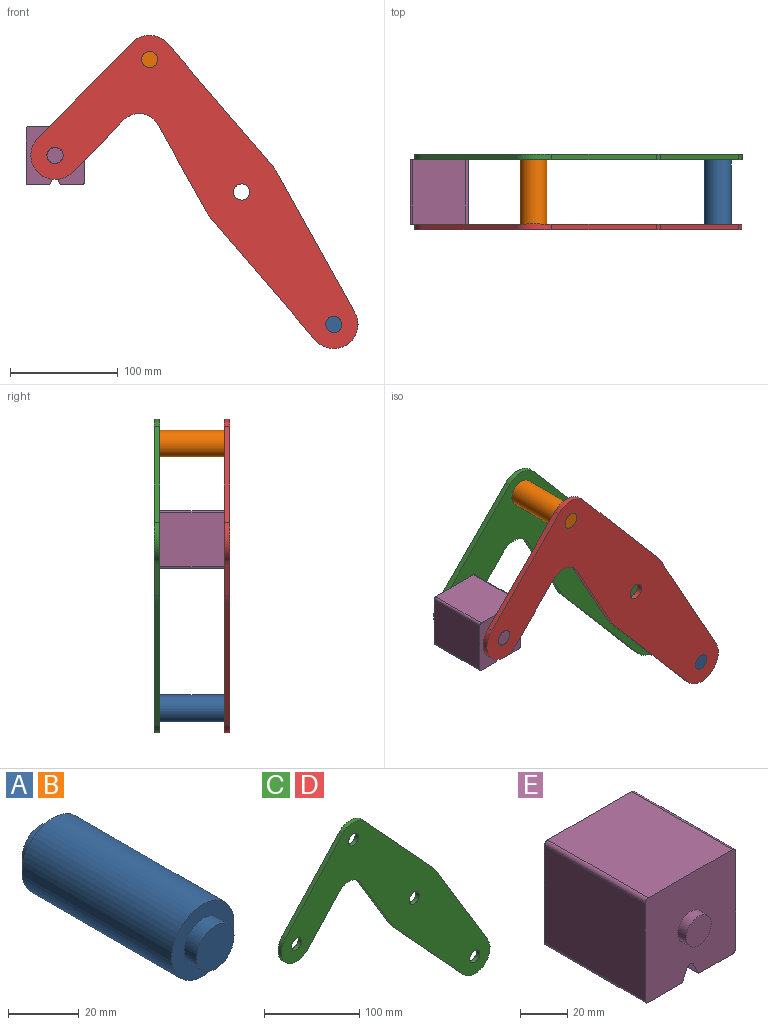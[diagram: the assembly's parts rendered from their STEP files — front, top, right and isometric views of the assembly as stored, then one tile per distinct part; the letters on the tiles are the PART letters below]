
ASSEMBLY  parts=5 mates=3
PART A: 7 faces, bbox 25x70x25 mm
  f0: cylinder r=12.5mm len=60mm, axis (0,-1,0), area 4712.4mm2, adj f2,f5
  f1: cylinder r=7.5mm len=15mm, axis (0,1,0), area 235.6mm2, adj f2,f3
  f2: plane 25x25mm, normal (0,-1,0), area 314.2mm2, adj f0,f1
  f3: plane 15x15mm, normal (0,-1,0), area 176.7mm2, adj f1
  f4: cylinder r=7.5mm len=15mm, axis (0,-1,0), area 235.6mm2, adj f5,f6
  f5: plane 25x25mm, normal (0,1,0), area 314.2mm2, adj f0,f4
  f6: plane 15x15mm, normal (0,1,0), area 176.7mm2, adj f4
PART B: same geometry as A
PART C: 18 faces, bbox 309.5x5x285.1 mm
  f0: cylinder r=22.5mm len=39.07mm, axis (0,1,0), area 353.4mm2, adj f1,f13,f16,f17
  f1: plane 50.28x46.21mm, normal (0.74,0,-0.68), area 341.4mm2, adj f0,f2,f16,f17
  f2: cylinder r=20mm len=31.85mm, axis (0,1,0), area 185.5mm2, adj f1,f3,f16,f17
  f3: plane 79.23x47.81mm, normal (-0.86,0,-0.52), area 462.7mm2, adj f2,f4,f16,f17
  f4: cylinder r=37.5mm len=6mm, axis (0,1,0), area 37.6mm2, adj f3,f5,f16,f17
  f5: plane 109.88x101mm, normal (-0.74,0,-0.68), area 746.2mm2, adj f4,f6,f16,f17
  f6: cylinder r=22.5mm len=39.07mm, axis (0,1,0), area 330.9mm2, adj f5,f7,f16,f17
  f7: plane 127.78x77.11mm, normal (0.86,0,0.52), area 746.2mm2, adj f6,f8,f16,f17
  f8: cylinder r=37.5mm len=6mm, axis (0,1,0), area 37.6mm2, adj f7,f9,f16,f17
  f9: plane 109.88x101mm, normal (0.74,0,0.68), area 746.2mm2, adj f8,f10,f16,f17
  f10: cylinder r=22.5mm len=33.13mm, axis (0,1,0), area 186.2mm2, adj f9,f13,f16,f17
  f11: cylinder r=7.5mm len=15mm, axis (0,1,0), area 235.6mm2, adj f16,f17
  f12: cylinder r=7.5mm len=15mm, axis (0,1,0), area 235.6mm2, adj f16,f17
  f13: plane 92.03x84.59mm, normal (-0.74,0,0.68), area 625mm2, adj f0,f10,f16,f17
  f14: cylinder r=7.5mm len=15mm, axis (0,1,0), area 235.6mm2, adj f16,f17
  f15: cylinder r=7.5mm len=15mm, axis (0,1,0), area 235.6mm2, adj f16,f17
  f16: plane 309.5x285.07mm, normal (0,-1,0), area 24555.4mm2, adj f0,f1,f2,f3,f4,f5,f6,f7
  f17: plane 309.5x285.07mm, normal (0,1,0), area 24555.4mm2, adj f0,f1,f2,f3,f4,f5,f6,f7
PART D: same geometry as C
PART E: 18 faces, bbox 54x70x54 mm
  f0: plane 60x50.01mm, normal (0,0,1), area 3000.4mm2, adj f4,f10,f13,f14
  f1: plane 60x50.01mm, normal (-1,0,0), area 3000.4mm2, adj f4,f10,f14,f15
  f2: plane 60x20mm, normal (0,0,-1), area 1200.2mm2, adj f3,f4,f10,f15
  f3: plane 60x6.42mm, normal (0.89,0,-0.45), area 430.8mm2, adj f2,f4,f10,f16
  f4: plane 54.01x54.01mm, normal (0,-1,0), area 2690.1mm2, adj f0,f1,f2,f3,f5,f6,f7,f9
  f5: plane 60x50.01mm, normal (1,0,0), area 3000.4mm2, adj f4,f10,f13,f17
  f6: plane 60x6.42mm, normal (-0.89,0,-0.45), area 430.8mm2, adj f4,f7,f10,f16
  f7: plane 60x20mm, normal (0,0,-1), area 1200.2mm2, adj f4,f6,f10,f17
  f8: plane 15x15mm, normal (0,-1,0), area 176.7mm2, adj f9
  f9: cylinder r=7.5mm len=15mm, axis (0,1,0), area 235.6mm2, adj f4,f8
  f10: plane 54.01x54.01mm, normal (0,1,0), area 2690.1mm2, adj f0,f1,f2,f3,f5,f6,f7,f12
  f11: plane 15x15mm, normal (0,1,0), area 176.7mm2, adj f12
  f12: cylinder r=7.5mm len=15mm, axis (0,-1,0), area 235.6mm2, adj f10,f11
  f13: cylinder r=2mm len=60mm, axis (0,-1,0), area 188.5mm2, adj f0,f4,f5,f10
  f14: cylinder r=2mm len=60mm, axis (0,1,0), area 188.5mm2, adj f0,f1,f4,f10
  f15: cylinder r=2mm len=60mm, axis (0,-1,0), area 188.5mm2, adj f1,f2,f4,f10
  f16: cylinder r=2mm len=60mm, axis (0,-1,0), area 265.7mm2, adj f3,f4,f6,f10
  f17: cylinder r=2mm len=60mm, axis (0,1,0), area 188.5mm2, adj f4,f5,f7,f10
PLACE A rot(axis=(0,1,0),2deg) t=(171.36,-30,-246.25)mm
PLACE B rot(axis=(0,1,0),2deg) t=(0,-30,0)mm
PLACE C rot(axis=(0,1,0),2deg) t=(0,35,0)mm
PLACE D rot(axis=(0,1,0),2deg) t=(0,-30,0)mm fixed
PLACE E t=(1.09,-30,5.71)mm
MATE fastened C.f10 <-> B.f0  axis (0,-1,0) through (-85.68,30,123.12)mm
MATE revolute D.f0 <-> E.f4  axis (0,1,0) through (-173.45,-30,34.12)mm
MATE fastened A.f0 <-> D.f6  axis (0,-1,0) through (85.68,-30,-123.12)mm
